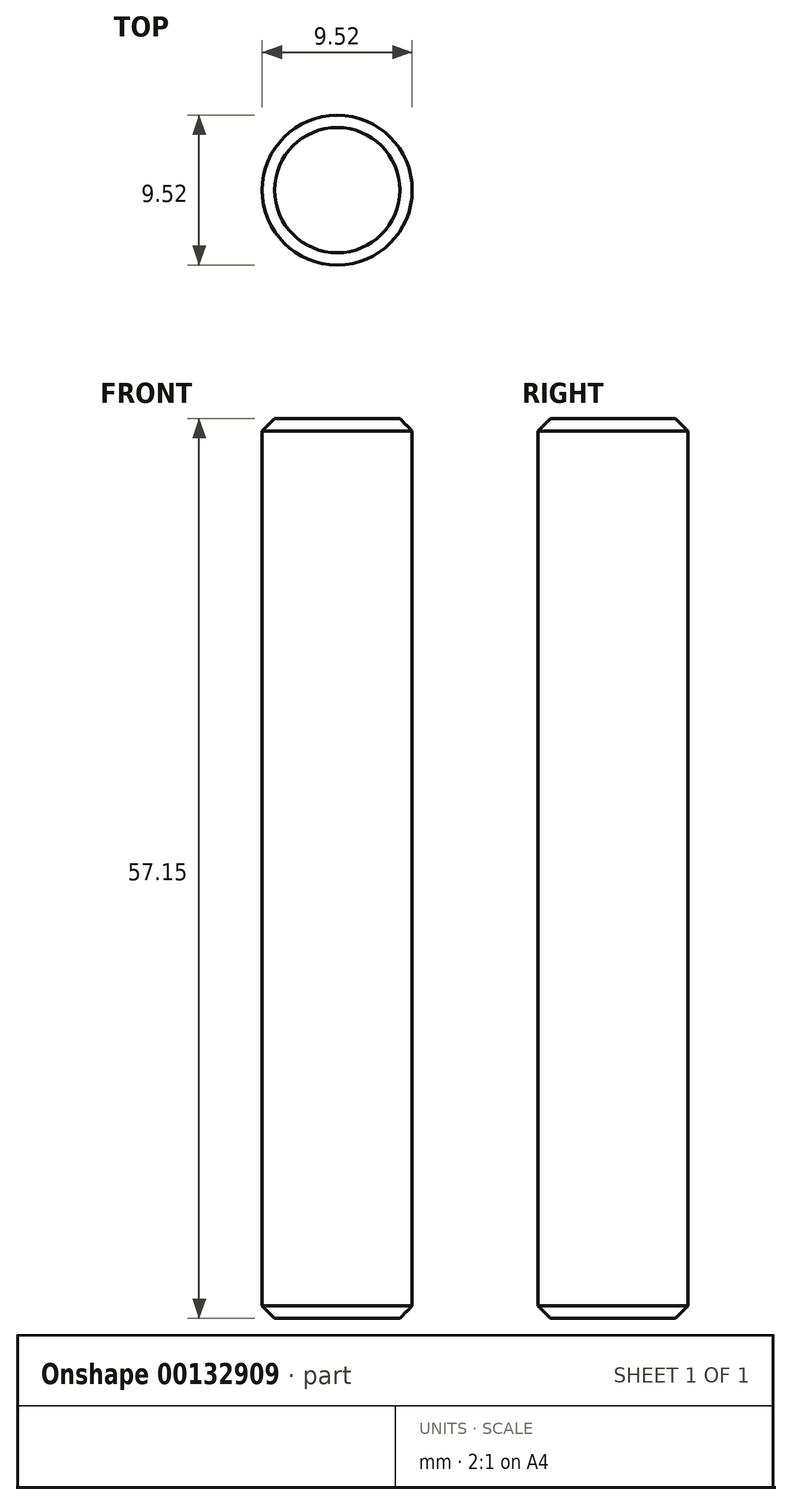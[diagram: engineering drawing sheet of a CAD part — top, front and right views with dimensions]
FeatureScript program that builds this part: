
annotation { "Feature Type Name" : "Feature", "Feature Type Description" : "" }
export const myFeature = defineFeature(function(context is Context, id is Id, definition is map)
    precondition{}
    {
        {
            var Q0;
            Q0=qCreatedBy(makeId("Top.planeOp"),FACE);
            var sketch = newSketch(context, id + "F0", { "sketchPlane" : qUnion([Q0])});
            skCircle(sketch, "E0", {"center": v(0, 0) * mm, "radius": 4.76 * mm});
            skSolve(sketch);
        }
        {
            var Q0;
            Q0=makeQuery(id+"F0.imprint","IMPRINT",FACE,{"disambiguationData":[TD([[makeQuery(id+"F0.imprint","IMPRINT",EDGE,{"derivedFrom":sQuery(id+"F0.wireOp",EDGE,"E0")}),1.0]])]});
            extrude(context, id + "F1", {"entities" : qUnion([Q0]), "oppositeDirection" : true, "depth" : 57.15 * mm});
        }
        {
            var Q0;
            Q0=makeQuery(id+"F1.opExtrude","CAP_EDGE",EDGE,{"disambiguationData":[OSD([sQuery(id+"F0.wireOp",EDGE,"E0")])],"isStart":true});
            var Q1;
            Q1=makeQuery(id+"F1.opExtrude","CAP_EDGE",EDGE,{"disambiguationData":[OSD([sQuery(id+"F0.wireOp",EDGE,"E0")])],"isStart":false});
            chamfer(context, id + "F2", {"entities" : qUnion([Q0, Q1]), "width" : 0.79 * mm, "tangentPropagation" : true});
        }
    });
